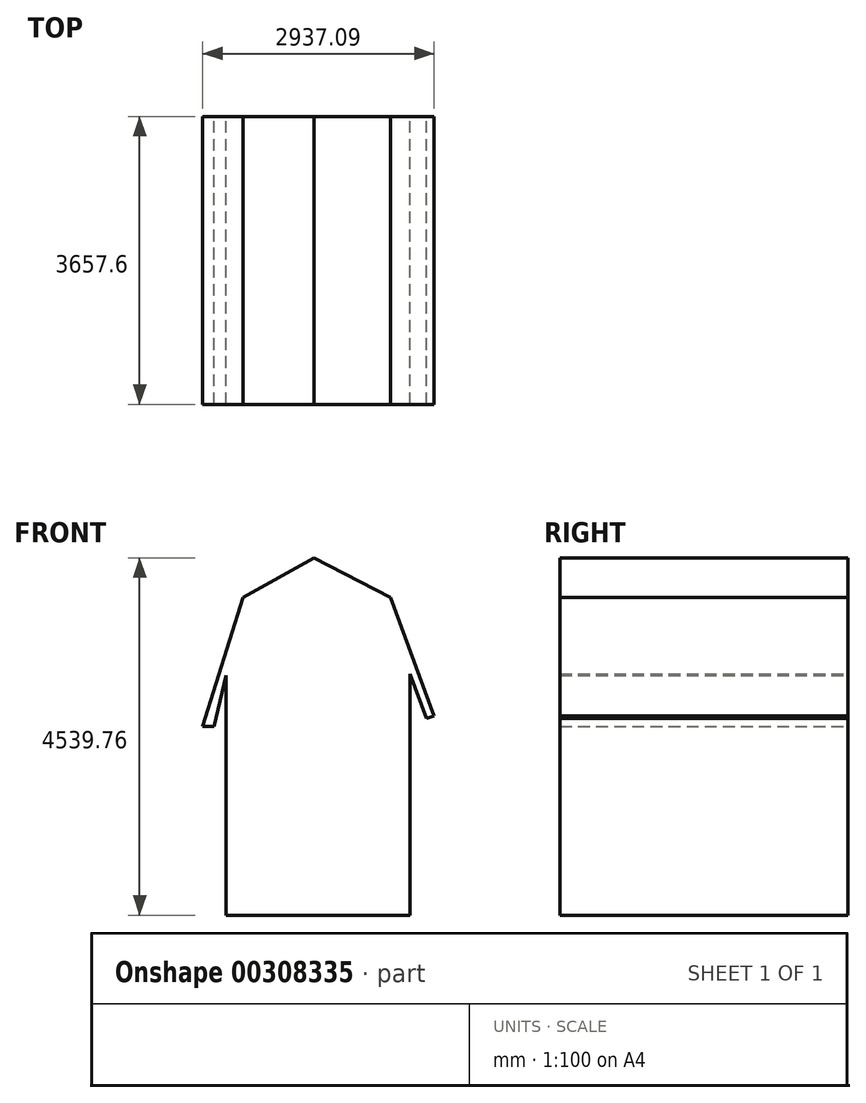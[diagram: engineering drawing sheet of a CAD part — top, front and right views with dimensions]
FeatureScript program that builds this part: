
annotation { "Feature Type Name" : "Feature", "Feature Type Description" : "" }
export const myFeature = defineFeature(function(context is Context, id is Id, definition is map)
    precondition{}
    {
        {
            var Q0;
            Q0=qCreatedBy(makeId("Front.planeOp"),FACE);
            var sketch = newSketch(context, id + "F0", { "sketchPlane" : qUnion([Q0])});
            skLineSegment(sketch, "E0.top", {"start": v(-1518.08, -1834.23) * mm, "end": v(819.95, -1834.23) * mm});
            skLineSegment(sketch, "E0.left", {"start": v(-1518.08, 1213.77) * mm, "end": v(-1518.08, -1834.23) * mm});
            skLineSegment(sketch, "E0.right", {"start": v(819.95, 1232.16) * mm, "end": v(819.95, -1834.23) * mm});
            skLineSegment(sketch, "E1", {"start": v(-1812.9, 560) * mm, "end": v(-1303.42, 2201.38) * mm});
            skLineSegment(sketch, "E2", {"start": v(-1303.42, 2201.38) * mm, "end": v(-397.89, 2705.53) * mm});
            skLineSegment(sketch, "E3", {"start": v(-397.89, 2705.53) * mm, "end": v(573, 2201.38) * mm});
            skLineSegment(sketch, "E4", {"start": v(573, 2201.38) * mm, "end": v(1124.18, 697) * mm});
            skLineSegment(sketch, "E5", {"start": v(1124.18, 697) * mm, "end": v(1028.83, 662.05) * mm});
            skLineSegment(sketch, "E6", {"start": v(1028.83, 662.05) * mm, "end": v(819.95, 1232.16) * mm});
            skLineSegment(sketch, "E7", {"start": v(-1518.08, 1213.77) * mm, "end": v(-1671.1, 560) * mm});
            skLineSegment(sketch, "E8", {"start": v(-1671.1, 560) * mm, "end": v(-1812.9, 560) * mm});
            skPoint(sketch, "E9.top.start.orphan", {"position": v(-1196.4, 0) * mm});
            skPoint(sketch, "E10.right.start.orphan", {"position": v(549.32, 0) * mm});
            skSolve(sketch);
        }
        {
            var Q0;
            Q0 = qSketchRegion(id + "F0", true);
            extrude(context, id + "F1", {"entities" : qUnion([Q0]), "depth" : 3657.6 * mm});
        }
    });
